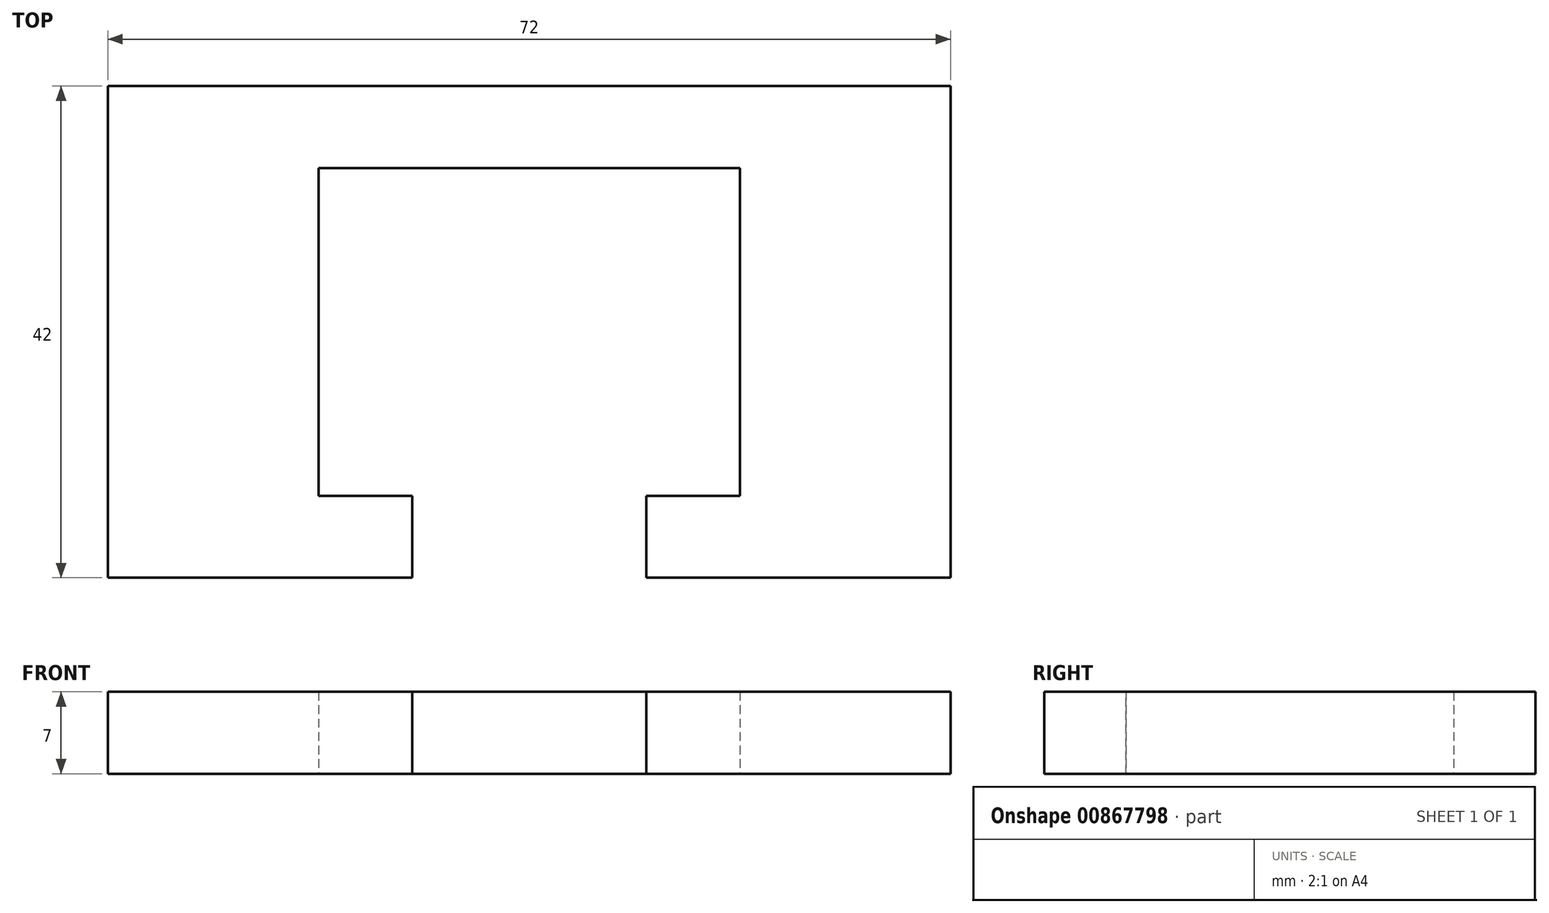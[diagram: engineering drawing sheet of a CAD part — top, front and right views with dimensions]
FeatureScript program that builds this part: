
annotation { "Feature Type Name" : "Feature", "Feature Type Description" : "" }
export const myFeature = defineFeature(function(context is Context, id is Id, definition is map)
    precondition{}
    {
        {
            var Q0;
            Q0=qCreatedBy(makeId("Top.planeOp"),FACE);
            var sketch = newSketch(context, id + "F0", { "sketchPlane" : qUnion([Q0])});
            skLineSegment(sketch, "E0.bottom", {"start": v(36, -21) * mm, "end": v(-36, -21) * mm});
            skLineSegment(sketch, "E0.top", {"start": v(36, 21) * mm, "end": v(-36, 21) * mm});
            skLineSegment(sketch, "E0.left", {"start": v(36, -21) * mm, "end": v(36, 21) * mm});
            skLineSegment(sketch, "E0.right", {"start": v(-36, -21) * mm, "end": v(-36, 21) * mm});
            skPoint(sketch, "E0.middle", {"position": v(0, 0) * mm});
            skLineSegment(sketch, "E1.bottom", {"start": v(18, -14) * mm, "end": v(-18, -14) * mm});
            skLineSegment(sketch, "E1.top", {"start": v(18, 14) * mm, "end": v(-18, 14) * mm});
            skLineSegment(sketch, "E1.left", {"start": v(18, -14) * mm, "end": v(18, 14) * mm});
            skLineSegment(sketch, "E1.right", {"start": v(-18, -14) * mm, "end": v(-18, 14) * mm});
            skLineSegment(sketch, "E2.bottom", {"start": v(10, -21) * mm, "end": v(-10, -21) * mm});
            skLineSegment(sketch, "E2.top", {"start": v(10, -14) * mm, "end": v(-10, -14) * mm});
            skLineSegment(sketch, "E2.left", {"start": v(10, -21) * mm, "end": v(10, -14) * mm});
            skLineSegment(sketch, "E2.right", {"start": v(-10, -21) * mm, "end": v(-10, -14) * mm});
            skPoint(sketch, "E2.middle", {"position": v(0, -17.5) * mm});
            skSolve(sketch);
        }
        {
            var Q0;
            Q0=makeQuery(id+"F0.imprint","IMPRINT",FACE,{"disambiguationData":[TD([[makeQuery(id+"F0.imprint","IMPRINT",EDGE,{"derivedFrom":sQuery(id+"F0.wireOp",EDGE,"E0.top")}),1.0]])]});
            extrude(context, id + "F1", {"entities" : qUnion([Q0]), "depth" : 7 * mm, "offsetDistance" : 25 * mm});
        }
    });
